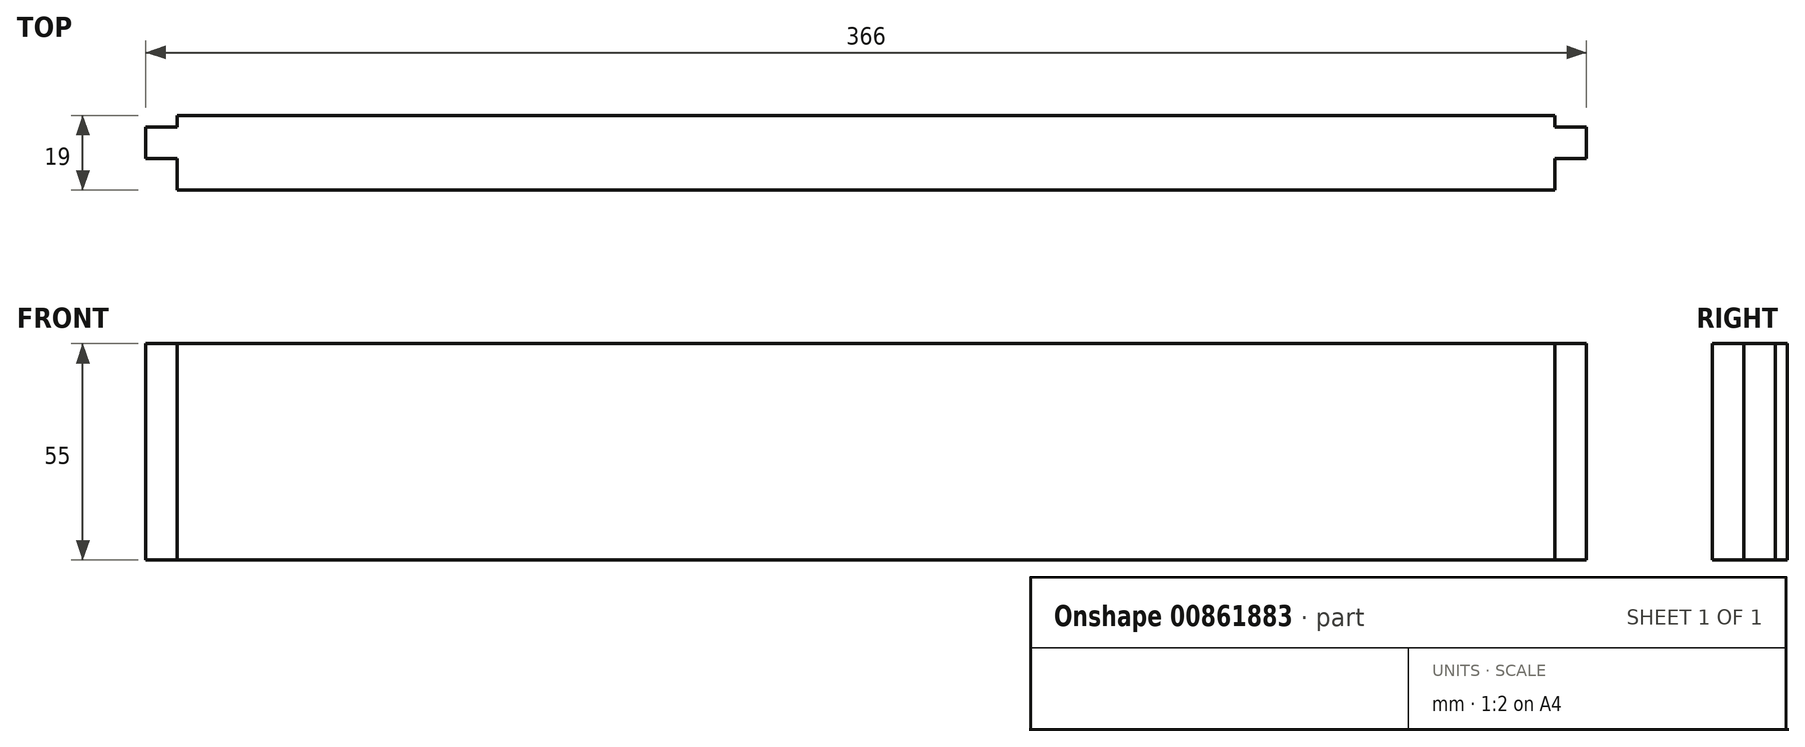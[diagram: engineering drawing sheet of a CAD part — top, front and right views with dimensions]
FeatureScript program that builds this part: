
annotation { "Feature Type Name" : "Feature", "Feature Type Description" : "" }
export const myFeature = defineFeature(function(context is Context, id is Id, definition is map)
    precondition{}
    {
        {
            var Q0;
            Q0=qCreatedBy(makeId("Front.planeOp"),FACE);
            var sketch = newSketch(context, id + "F0", { "sketchPlane" : qUnion([Q0])});
            skLineSegment(sketch, "E0.bottom", {"start": v(-183, 27.5) * mm, "end": v(183, 27.5) * mm});
            skLineSegment(sketch, "E0.top", {"start": v(-183, -27.5) * mm, "end": v(183, -27.5) * mm});
            skLineSegment(sketch, "E0.left", {"start": v(-183, 27.5) * mm, "end": v(-183, -27.5) * mm});
            skLineSegment(sketch, "E0.right", {"start": v(183, 27.5) * mm, "end": v(183, -27.5) * mm});
            skPoint(sketch, "E0.middle", {"position": v(0, 0) * mm});
            skSolve(sketch);
        }
        {
            var Q0;
            Q0 = qSketchRegion(id + "F0", true);
            extrude(context, id + "F1", {"entities" : qUnion([Q0]), "depth" : 19 * mm, "offsetDistance" : 25 * mm});
        }
        {
            var Q0;
            Q0=makeQuery(id+"F1.opExtrude","SWEPT_FACE",FACE,{"disambiguationData":[OSD([sQuery(id+"F0.wireOp",EDGE,"E0.right")])]});
            var sketch = newSketch(context, id + "F2", { "sketchPlane" : qUnion([Q0])});
            skLineSegment(sketch, "E1", {"start": v(-19, -27.5) * mm, "end": v(-11, -27.5) * mm});
            skLineSegment(sketch, "E2", {"start": v(-11, -27.5) * mm, "end": v(-11, 27.5) * mm});
            skLineSegment(sketch, "E3", {"start": v(-11, 27.5) * mm, "end": v(-3, 27.5) * mm});
            skLineSegment(sketch, "E4", {"start": v(-3, 27.5) * mm, "end": v(-3, -27.5) * mm});
            skSolve(sketch);
        }
        {
            var Q0;
            Q0=makeQuery(id+"F2.imprint","IMPRINT",FACE,{"disambiguationData":[TD([[makeQuery(id+"F2.imprint","IMPRINT",EDGE,{"derivedFrom":sQuery(id+"F2.wireOp",EDGE,"E1")}),1.0]])]});
            var Q1;
            {var subQ0=sQuery(id+"F2.wireOp",EDGE,"E4");Q1=makeQuery(id+"F2.imprint","IMPRINT",FACE,{"disambiguationData":[TD([[makeQuery(id+"F2.imprint","IMPRINT",EDGE,{"derivedFrom":subQ0}),1.0]])]});}
            extrude(context, id + "F3", {"entities" : qUnion([Q0, Q1]), "operationType" : NewBodyOperationType.REMOVE, "oppositeDirection" : true, "depth" : 8 * mm, "offsetDistance" : 25 * mm});
        }
        {
            var Q0;
            Q0=makeQuery(id+"F1.opExtrude","SWEPT_FACE",FACE,{"disambiguationData":[OSD([sQuery(id+"F0.wireOp",EDGE,"E0.left")])]});
            var sketch = newSketch(context, id + "F4", { "sketchPlane" : qUnion([Q0])});
            skLineSegment(sketch, "E5", {"start": v(19, -27.5) * mm, "end": v(11, -27.5) * mm});
            skLineSegment(sketch, "E6", {"start": v(11, -27.5) * mm, "end": v(11, 27.5) * mm});
            skLineSegment(sketch, "E7", {"start": v(11, 27.5) * mm, "end": v(3, 27.5) * mm});
            skLineSegment(sketch, "E8", {"start": v(3, 27.5) * mm, "end": v(3, -27.5) * mm});
            skSolve(sketch);
        }
        {
            var Q0;
            Q0=makeQuery(id+"F4.imprint","IMPRINT",FACE,{"disambiguationData":[TD([[makeQuery(id+"F4.imprint","IMPRINT",EDGE,{"derivedFrom":sQuery(id+"F4.wireOp",EDGE,"E5")}),-1.0]])]});
            var Q1;
            {var subQ0=sQuery(id+"F4.wireOp",EDGE,"E8");Q1=makeQuery(id+"F4.imprint","IMPRINT",FACE,{"disambiguationData":[TD([[makeQuery(id+"F4.imprint","IMPRINT",EDGE,{"derivedFrom":subQ0}),-1.0]])]});}
            extrude(context, id + "F5", {"entities" : qUnion([Q0, Q1]), "operationType" : NewBodyOperationType.REMOVE, "oppositeDirection" : true, "depth" : 8 * mm, "offsetDistance" : 25 * mm});
        }
    });
